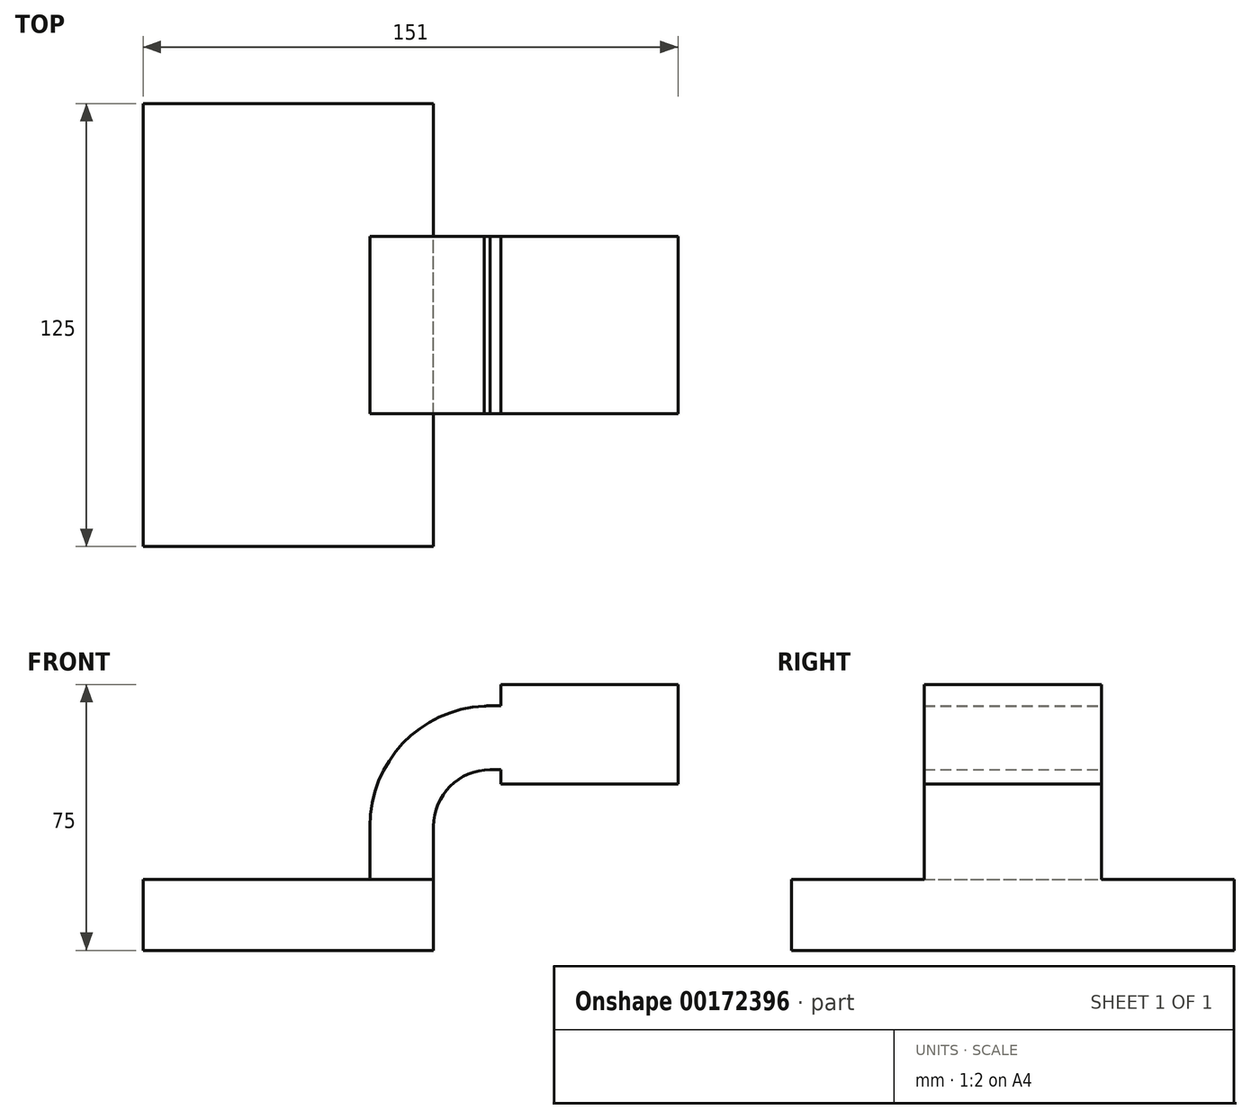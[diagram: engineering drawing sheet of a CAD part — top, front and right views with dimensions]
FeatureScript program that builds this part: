
annotation { "Feature Type Name" : "Feature", "Feature Type Description" : "" }
export const myFeature = defineFeature(function(context is Context, id is Id, definition is map)
    precondition{}
    {
        {
            var Q0;
            Q0=qCreatedBy(makeId("Front.planeOp"),FACE);
            var sketch = newSketch(context, id + "F0", { "sketchPlane" : qUnion([Q0])});
            skLineSegment(sketch, "E0.bottom", {"start": v(-41, -10) * mm, "end": v(41, -10) * mm});
            skLineSegment(sketch, "E0.top", {"start": v(-41, 10) * mm, "end": v(41, 10) * mm});
            skLineSegment(sketch, "E0.left", {"start": v(-41, -10) * mm, "end": v(-41, 10) * mm});
            skLineSegment(sketch, "E0.right", {"start": v(41, -10) * mm, "end": v(41, 10) * mm});
            skPoint(sketch, "E0.middle", {"position": v(0, 0) * mm});
            skLineSegment(sketch, "E1.bottom", {"start": v(60, 37) * mm, "end": v(110, 37) * mm});
            skLineSegment(sketch, "E1.top", {"start": v(60, 65) * mm, "end": v(110, 65) * mm});
            skLineSegment(sketch, "E1.left", {"start": v(60, 37) * mm, "end": v(60, 65) * mm});
            skLineSegment(sketch, "E1.right", {"start": v(110, 37) * mm, "end": v(110, 65) * mm});
            skPoint(sketch, "E1.middle", {"position": v(85, 51) * mm});
            skLineSegment(sketch, "E2", {"start": v(41, 10) * mm, "end": v(41, 25) * mm});
            skArc(sketch, "E3", {"start": v(41, 25) * mm, "mid": v(45.69, 36.31) * mm, "end": v(57, 41) * mm});
            skLineSegment(sketch, "E4", {"start": v(57, 41) * mm, "end": v(81.23, 41) * mm});
            skLineSegment(sketch, "E5.0", {"start": v(57, 59) * mm, "end": v(81.23, 59) * mm});
            skArc(sketch, "E5.1", {"start": v(23, 25) * mm, "mid": v(32.96, 49.04) * mm, "end": v(57, 59) * mm});
            skLineSegment(sketch, "E5.2", {"start": v(23, 10) * mm, "end": v(23, 25) * mm});
            skLineSegment(sketch, "E6", {"start": v(81.23, 41) * mm, "end": v(81.23, 59) * mm});
            skFitSpline(sketch, "E7", {"points": [v(-41, 10) * mm, v(57, 59) * mm], "startDerivative": vector(-0.83, 85.27) * mm, "endDerivative": vector(120.5, 2.23) * mm});
            skSolve(sketch);
        }
        {
            var Q0;
            Q0=makeQuery(id+"F0.imprint","IMPRINT",FACE,{"disambiguationData":[TD([[makeQuery(id+"F0.imprint","IMPRINT",EDGE,{"derivedFrom":sQuery(id+"F0.wireOp",EDGE,"E0.bottom")}),1.0]])]});
            extrude(context, id + "F1", {"entities" : qUnion([Q0]), "endBound" : BoundingType.SYMMETRIC, "depth" : 125 * mm});
        }
        {
            var Q0;
            {var subQ1=sQuery(id+"F0.wireOp",EDGE,"E2");Q0=makeQuery(id+"F0.imprint","IMPRINT",FACE,{"disambiguationData":[TD([[makeQuery(id+"F0.imprint","IMPRINT",EDGE,{"derivedFrom":subQ1}),1.0]])]});}
            var Q1;
            {var subQ5=sQuery(id+"F0.wireOp",EDGE,"E6");Q1=makeQuery(id+"F0.imprint","IMPRINT",FACE,{"disambiguationData":[TD([[makeQuery(id+"F0.imprint","IMPRINT",EDGE,{"derivedFrom":subQ5}),1.0]])]});}
            var Q2;
            {var subQ4=sQuery(id+"F0.wireOp",EDGE,"E1.bottom");Q2=makeQuery(id+"F0.imprint","IMPRINT",FACE,{"disambiguationData":[TD([[makeQuery(id+"F0.imprint","IMPRINT",EDGE,{"derivedFrom":subQ4}),1.0]])]});}
            extrude(context, id + "F2", {"entities" : qUnion([Q0, Q1, Q2]), "operationType" : NewBodyOperationType.ADD, "endBound" : BoundingType.SYMMETRIC, "depth" : 50 * mm});
        }
    });
